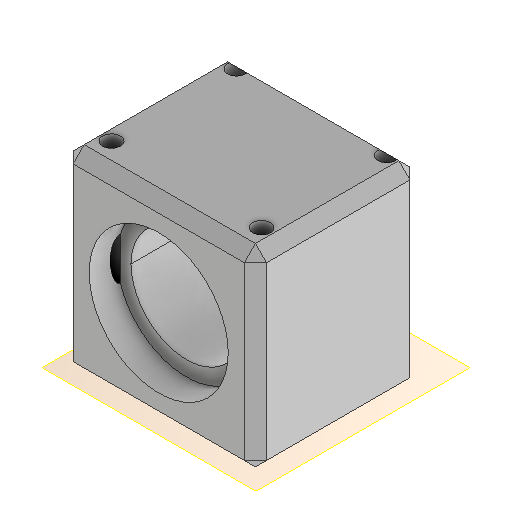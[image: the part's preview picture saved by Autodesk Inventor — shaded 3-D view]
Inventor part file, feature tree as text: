
AUTODESK INVENTOR PART (.ipt)
format: ipt  version: 2024.1 (Build 281209000, 209)  size: 185,344 bytes
history: native  units: mm
features: extrude x3, sketch x3, reference x3, other x3, plane x1, chamfer x1, mirror x1
ambient origin geometry x8: Origin, YZ Plane, XZ Plane, XY Plane, X Axis, Y Axis, Z Axis, Center Point
bodies: Volumenkörper1 (feature_tree)
feature tree (15):
  plane  "Arbeitsebene1"
  extrude  "Extrusion1"  Depth=34.8mm
  extrude  "Extrusion2"  Depth=17.4mm TaperAngle=0.0deg
  extrude  "Extrusion3"  Depth=5.0mm TaperAngle=0.0deg
  chamfer  "Fasen1"  Distance=20.0mm
  mirror  "Spiegeln1"
  sketch  "Skizze1"  dims[d0=34.8mm d1=30.0mm]
  reference  "Referenz1"
  sketch  "Skizze2"  dims[d2=2.3mm d3=17.4mm d4=0.0mm]
  reference  "Referenz2"
  sketch  "Skizze3"  dims[d5=25.0mm d6=5.0mm d7=0.0mm d8=20.0mm d9=0.0mm d10=0.0mm d11=2.0mm d12=2.0mm d13=45.0deg]
  reference  "Referenz3"
  other  "Assembly_MicroscopeInABox_v0.iam"
  other  "MIAB_Case_v0:1"
  other  "00_10x_Objective_ViewSolutions_bm05073332:1"
